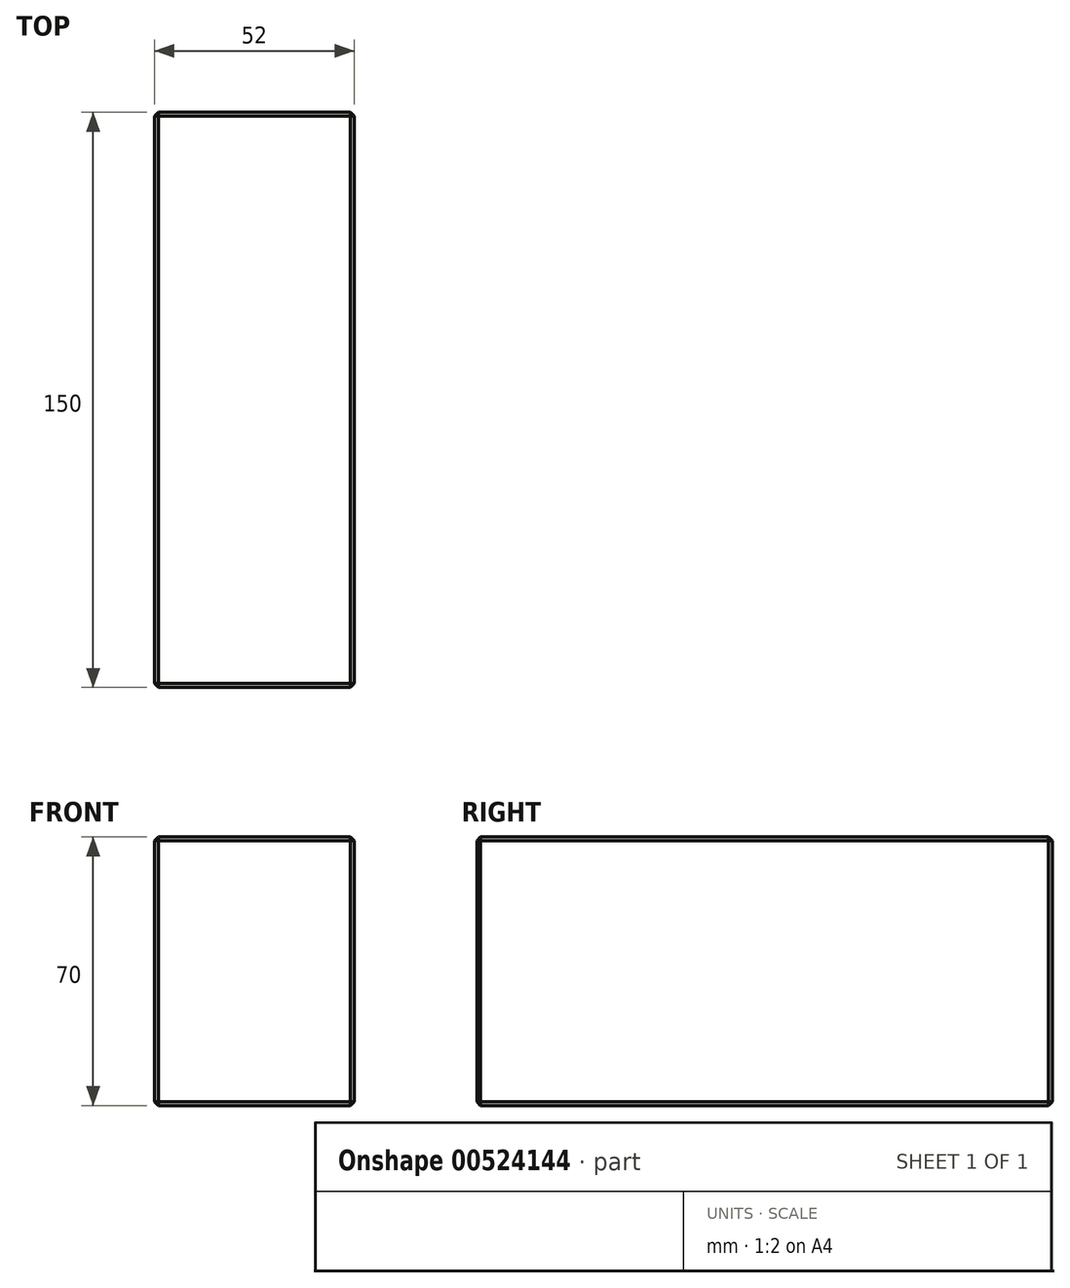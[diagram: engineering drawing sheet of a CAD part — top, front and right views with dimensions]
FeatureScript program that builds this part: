
annotation { "Feature Type Name" : "Feature", "Feature Type Description" : "" }
export const myFeature = defineFeature(function(context is Context, id is Id, definition is map)
    precondition{}
    {
        {
            var Q0;
            Q0=qCreatedBy(makeId("Top.planeOp"),FACE);
            var sketch = newSketch(context, id + "F0", { "sketchPlane" : qUnion([Q0])});
            skLineSegment(sketch, "E0.bottom", {"start": v(26, -75) * mm, "end": v(-26, -75) * mm});
            skLineSegment(sketch, "E0.top", {"start": v(26, 75) * mm, "end": v(-26, 75) * mm});
            skLineSegment(sketch, "E0.left", {"start": v(26, -75) * mm, "end": v(26, 75) * mm});
            skLineSegment(sketch, "E0.right", {"start": v(-26, -75) * mm, "end": v(-26, 75) * mm});
            skPoint(sketch, "E0.middle", {"position": v(0, 0) * mm});
            skSolve(sketch);
        }
        {
            var Q0;
            Q0=qSketchRegion(id+"F0",true);
            extrude(context, id + "F1", {"entities" : qUnion([Q0]), "depth" : 70 * mm});
        }
        {
            var Q0;
            Q0=makeQuery(id+"F1.opExtrude","CAP_EDGE",EDGE,{"disambiguationData":[OSD([sQuery(id+"F0.wireOp",EDGE,"E0.bottom")])],"isStart":false});
            var Q1;
            Q1=makeQuery(id+"F1.opExtrude","SWEPT_EDGE",EDGE,{"disambiguationData":[OSD([sQuery(id+"F0.wireOp",EDGE,"E0.bottom"),sQuery(id+"F0.wireOp",EDGE,"E0.right")])]});
            var Q2;
            Q2=makeQuery(id+"F1.opExtrude","SWEPT_FACE",FACE,{"disambiguationData":[OSD([sQuery(id+"F0.wireOp",EDGE,"E0.bottom")])]});
            var Q3;
            Q3=makeQuery(id+"F1.opExtrude","CAP_EDGE",EDGE,{"disambiguationData":[OSD([sQuery(id+"F0.wireOp",EDGE,"E0.right")])],"isStart":true});
            var Q4;
            Q4=makeQuery(id+"F1.opExtrude","CAP_EDGE",EDGE,{"disambiguationData":[OSD([sQuery(id+"F0.wireOp",EDGE,"E0.left")])],"isStart":true});
            var Q5;
            Q5=makeQuery(id+"F1.opExtrude","CAP_EDGE",EDGE,{"disambiguationData":[OSD([sQuery(id+"F0.wireOp",EDGE,"E0.right")])],"isStart":false});
            var Q6;
            Q6=makeQuery(id+"F1.opExtrude","CAP_EDGE",EDGE,{"disambiguationData":[OSD([sQuery(id+"F0.wireOp",EDGE,"E0.left")])],"isStart":false});
            var Q7;
            Q7=makeQuery(id+"F1.opExtrude","CAP_EDGE",EDGE,{"disambiguationData":[OSD([sQuery(id+"F0.wireOp",EDGE,"E0.top")])],"isStart":true});
            var Q8;
            Q8=makeQuery(id+"F1.opExtrude","SWEPT_FACE",FACE,{"disambiguationData":[OSD([sQuery(id+"F0.wireOp",EDGE,"E0.top")])]});
            chamfer(context, id + "F2", {"entities" : qUnion([Q0, Q1, Q2, Q3, Q4, Q5, Q6, Q7, Q8]), "width" : 1 * mm, "tangentPropagation" : true});
        }
    });
